# Revit family: Противопожарный клапан KZO-2K
name_source: partatom
category: Оборудование
units: mm (PartAtom-declared; Revit-internal decimal feet)

## family parameters
Всегда вертикально = Да
Заголовок OmniClass = HVAC Distribution Devices
Классификация = Нет
На основе рабочей плоскости = Нет
Номер OmniClass = 23.75.70.00
Общий = Нет
При загрузке вырезать с полостями = Нет
Размер круглого соединителя = Использовать диаметр
Тип детали = Нормальный
Точка расчета площади = Нет

## types (1)
- Противопожарный клапан KZO-2K
    0 = ╂ : 0
    120 мин = ╃ : 120 мин
    60 мин = ╃ : 60 мин
    90 мин = ╃ : 90 мин
    ADSK_Единица измерения = шт.
    ADSK_Завод-изготовитель = ВЕРТРО
    ADSK_Классификация нагрузок = ОВК
    ADSK_Количество = 1
    ADSK_Количество фаз = 3
    ADSK_Коэффициент мощности = 1
    ADSK_Масса = 13.6
    ADSK_Масса_Текст = 13.6 кг
    ADSK_Материал = ВЕРТРО_Алюминий
    ADSK_Наименование = Противопожарный клапан
    ADSK_Наименование краткое = Противопожарный клапан KZO-2K
    ADSK_Напряжение = 220 В
    ADSK_Номинальная мощность = 5 Вт
    ADSK_Полная мощность = 5 В·А
    ADSK_Свободный напор воздуха = 0.0 Па
    F = ┿ : F
    LT = KZO-2K
    M = ╀ : S
    N = ┿ : F
    S = ╀ : S
    T = ╁ : T
    X = ╁ : T
    Z = ╂ : 0
    Отметка по умолчанию = 0 мм
